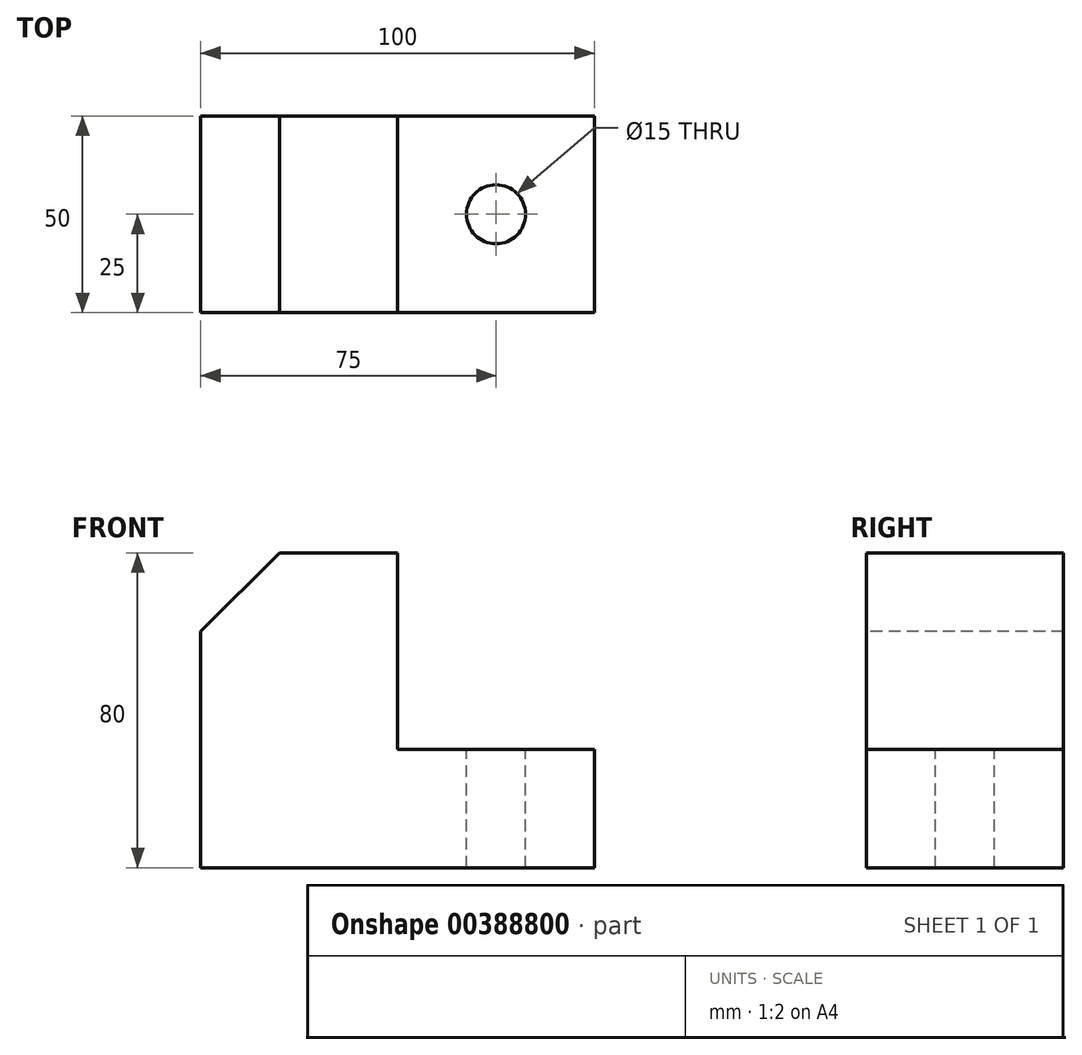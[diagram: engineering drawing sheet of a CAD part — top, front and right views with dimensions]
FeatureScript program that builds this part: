
annotation { "Feature Type Name" : "Feature", "Feature Type Description" : "" }
export const myFeature = defineFeature(function(context is Context, id is Id, definition is map)
    precondition{}
    {
        {
            var Q0;
            Q0=qCreatedBy(makeId("Top.planeOp"),FACE);
            var sketch = newSketch(context, id + "F0", { "sketchPlane" : qUnion([Q0])});
            skLineSegment(sketch, "E0.bottom", {"start": v(0, 0) * mm, "end": v(100, 0) * mm});
            skLineSegment(sketch, "E0.top", {"start": v(0, 50) * mm, "end": v(100, 50) * mm});
            skLineSegment(sketch, "E0.left", {"start": v(0, 0) * mm, "end": v(0, 50) * mm});
            skLineSegment(sketch, "E0.right", {"start": v(100, 0) * mm, "end": v(100, 50) * mm});
            skSolve(sketch);
        }
        {
            var Q0;
            Q0=makeQuery(id+"F0.imprint","IMPRINT",FACE,{"disambiguationData":[TD([[makeQuery(id+"F0.imprint","IMPRINT",EDGE,{"derivedFrom":sQuery(id+"F0.wireOp",EDGE,"E0.bottom")}),1.0]])]});
            extrude(context, id + "F1", {"entities" : qUnion([Q0]), "depth" : 80 * mm});
        }
        {
            var Q0;
            Q0=makeQuery(id+"F1.opExtrude","SWEPT_FACE",FACE,{"disambiguationData":[OSD([sQuery(id+"F0.wireOp",EDGE,"E0.bottom")])]});
            var sketch = newSketch(context, id + "F2", { "sketchPlane" : qUnion([Q0])});
            skLineSegment(sketch, "E1.bottom", {"start": v(50, 80) * mm, "end": v(100, 80) * mm});
            skLineSegment(sketch, "E1.top", {"start": v(50, 30) * mm, "end": v(100, 30) * mm});
            skLineSegment(sketch, "E1.left", {"start": v(50, 80) * mm, "end": v(50, 30) * mm});
            skLineSegment(sketch, "E1.right", {"start": v(100, 80) * mm, "end": v(100, 30) * mm});
            skSolve(sketch);
        }
        {
            var Q0;
            Q0=makeQuery(id+"F2.imprint","IMPRINT",FACE,{"disambiguationData":[TD([[makeQuery(id+"F2.imprint","IMPRINT",EDGE,{"derivedFrom":sQuery(id+"F2.wireOp",EDGE,"E1.bottom")}),-1.0]])]});
            extrude(context, id + "F3", {"entities" : qUnion([Q0]), "operationType" : NewBodyOperationType.REMOVE, "oppositeDirection" : true, "depth" : 102 * mm});
        }
        {
            var Q0;
            Q0=makeQuery(id+"F1.opExtrude","SWEPT_FACE",FACE,{"disambiguationData":[OSD([sQuery(id+"F0.wireOp",EDGE,"E0.bottom")])]});
            var sketch = newSketch(context, id + "F4", { "sketchPlane" : qUnion([Q0])});
            skLineSegment(sketch, "E2", {"start": v(20, 80) * mm, "end": v(0, 60) * mm});
            skSolve(sketch);
        }
        {
            var Q0;
            {var subQ0=sQuery(id+"F4.wireOp",EDGE,"E2");Q0=makeQuery(id+"F4.imprint","IMPRINT",FACE,{"disambiguationData":[TD([[makeQuery(id+"F4.imprint","IMPRINT",EDGE,{"derivedFrom":subQ0}),-1.0]])]});}
            extrude(context, id + "F5", {"entities" : qUnion([Q0]), "operationType" : NewBodyOperationType.REMOVE, "oppositeDirection" : true, "depth" : 92 * mm});
        }
        {
            var Q0;
            Q0=makeQuery(id+"F3.boolean.opBoolean","COPY",FACE,{"derivedFrom":makeQuery(id+"F3.opExtrude","SWEPT_FACE",FACE,{"disambiguationData":[OSD([sQuery(id+"F2.wireOp",EDGE,"E1.top")])]})});
            var sketch = newSketch(context, id + "F6", { "sketchPlane" : qUnion([Q0])});
            skCircle(sketch, "E3", {"center": v(75, 25) * mm, "radius": 7.5 * mm});
            skPoint(sketch, "E3.centerSnap0", {"position": v(75, 0) * mm});
            skPoint(sketch, "E3.centerSnap1", {"position": v(100, 25) * mm});
            skSolve(sketch);
        }
        {
            var Q0;
            Q0=makeQuery(id+"F6.imprint","IMPRINT",FACE,{"disambiguationData":[TD([[makeQuery(id+"F6.imprint","IMPRINT",EDGE,{"derivedFrom":sQuery(id+"F6.wireOp",EDGE,"E3")}),1.0]])]});
            extrude(context, id + "F7", {"entities" : qUnion([Q0]), "operationType" : NewBodyOperationType.REMOVE, "oppositeDirection" : true, "depth" : 64.2 * mm});
        }
    });
